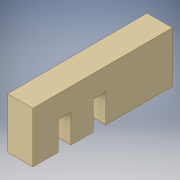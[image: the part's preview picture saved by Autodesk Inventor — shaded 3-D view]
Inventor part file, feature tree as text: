
AUTODESK INVENTOR PART (.ipt)
format: ipt  version: 2016 (Build 200138000, 138)  size: 105,472 bytes
history: native  units: in
note: dims shown in document units (in); Inventor stores cm internally (conversion verified against a paired STEP export)
features: extrude x2, sketch x2
ambient origin geometry x8: Origin, YZ Plane, XZ Plane, XY Plane, X Axis, Y Axis, Z Axis, Center Point
bodies: Solid1 (feature_tree)
feature tree (4):
  extrude  "Extrusion1"  Depth=4.0in
  extrude  "Extrusion2"  Depth=1.0in
  sketch  "Sketch1"  dims[d0=2.0in d1=4.0in]
  sketch  "Sketch2"  dims[d2=11.0in d3=0.0in d4=1.0in d5=2.25in d6=2.0in d7=1.0in d8=1.75in d9=10.5in d10=0.0in]
